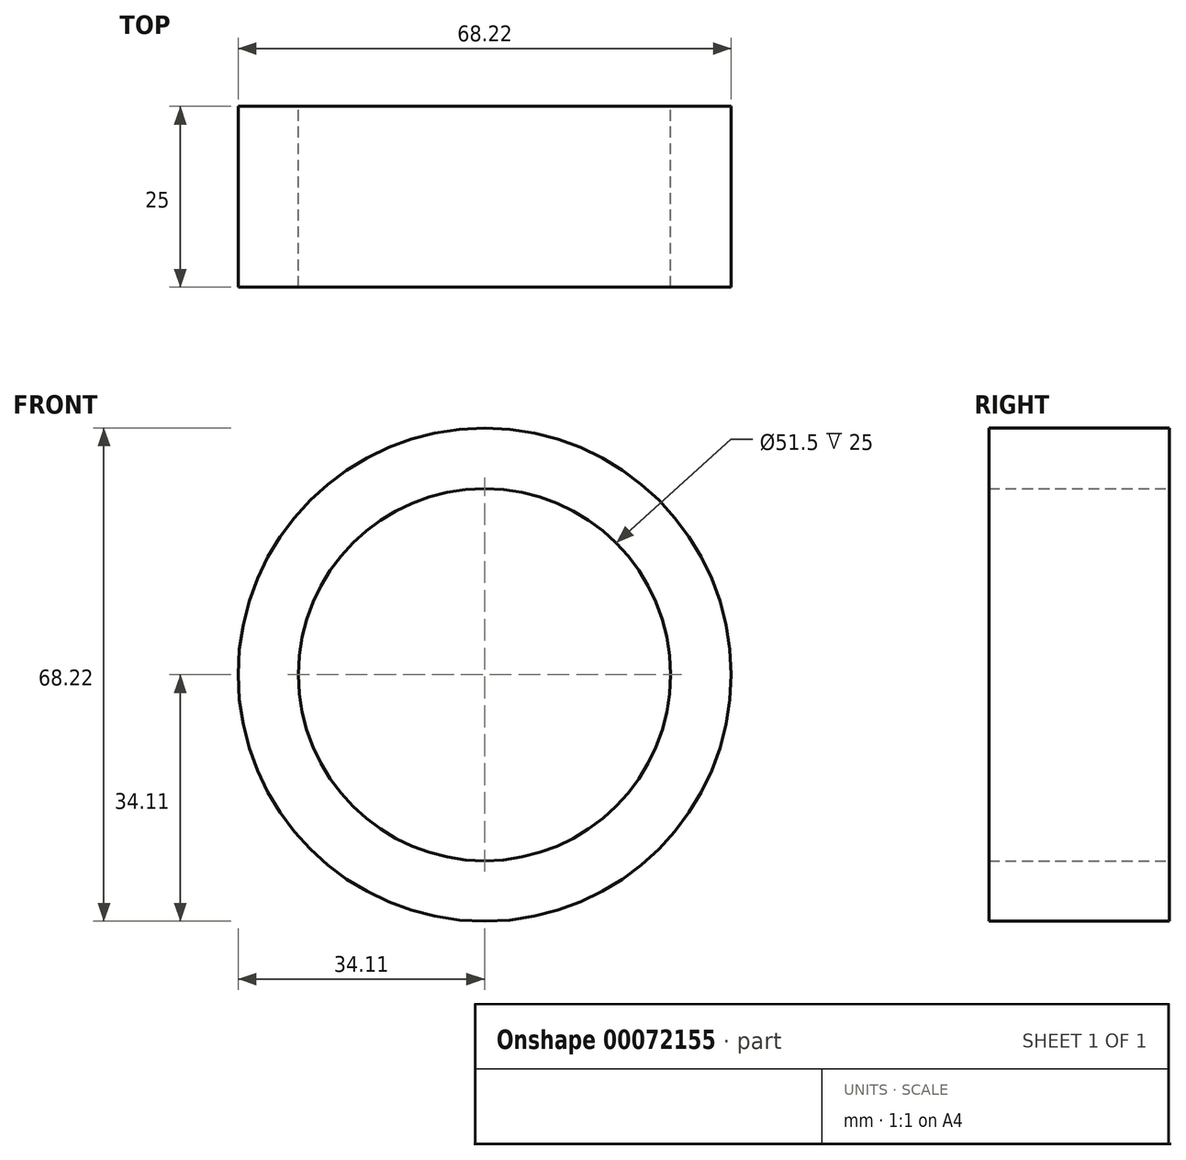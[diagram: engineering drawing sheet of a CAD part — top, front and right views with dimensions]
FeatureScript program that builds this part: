
annotation { "Feature Type Name" : "Feature", "Feature Type Description" : "" }
export const myFeature = defineFeature(function(context is Context, id is Id, definition is map)
    precondition{}
    {
        {
            var Q0;
            Q0=qCreatedBy(makeId("Front.planeOp"),FACE);
            var sketch = newSketch(context, id + "F0", { "sketchPlane" : qUnion([Q0])});
            skCircle(sketch, "E0", {"center": v(0, 0) * mm, "radius": 34.1 * mm});
            skCircle(sketch, "E1", {"center": v(0, 0) * mm, "radius": 25.75 * mm});
            skCircle(sketch, "E2", {"center": v(0, 0) * mm, "radius": 20.73 * mm});
            skCircle(sketch, "E3", {"center": v(0, 0) * mm, "radius": 6.97 * mm});
            skLineSegment(sketch, "E4", {"start": v(-5.1, 4.75) * mm, "end": v(5.1, 4.75) * mm});
            skLineSegment(sketch, "E5", {"start": v(-5.1, -4.75) * mm, "end": v(5.1, -4.75) * mm});
            skLineSegment(sketch, "E6", {"start": v(-2.2, 20.6) * mm, "end": v(-2.2, 6.62) * mm});
            skLineSegment(sketch, "E7", {"start": v(2.2, 6.62) * mm, "end": v(2.2, 20.6) * mm});
            skSolve(sketch);
        }
        {
            var Q0;
            Q0 = qSketchRegion(id + "F0", true);
            extrude(context, id + "F1", {"entities" : qUnion([Q0]), "depth" : 25 * mm});
        }
    });
